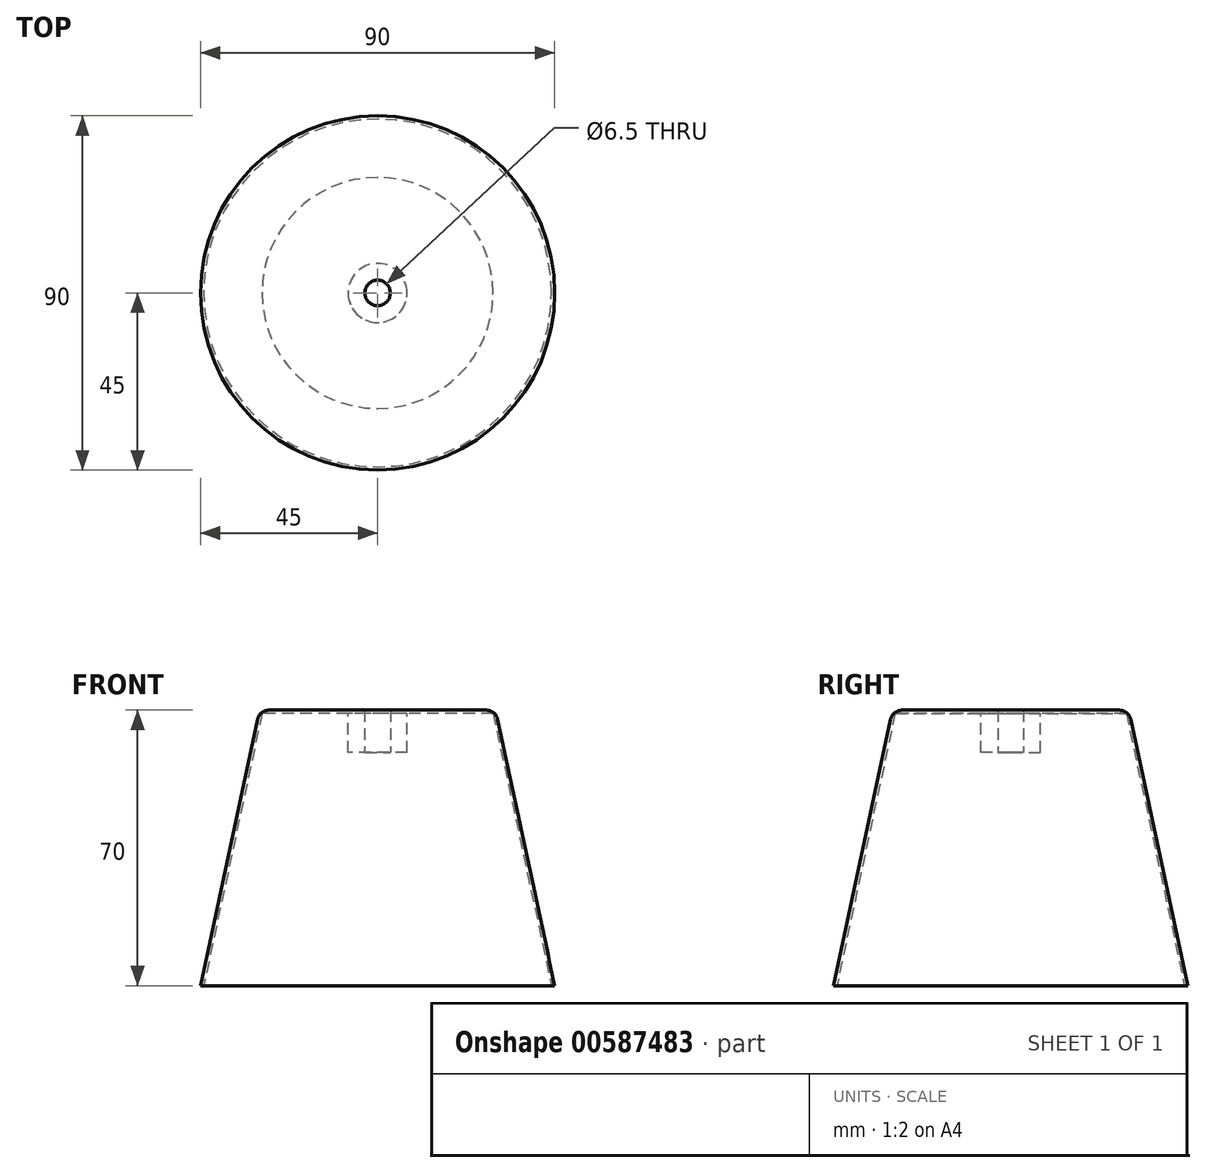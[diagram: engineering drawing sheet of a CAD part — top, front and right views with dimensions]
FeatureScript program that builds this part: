
annotation { "Feature Type Name" : "Feature", "Feature Type Description" : "" }
export const myFeature = defineFeature(function(context is Context, id is Id, definition is map)
    precondition{}
    {
        {
            var Q0;
            Q0=qCreatedBy(makeId("Top.planeOp"),FACE);
            cPlane(context, id + "F0", {"entities" : qUnion([Q0]), "cplaneType" : CPlaneType.OFFSET, "offset" : 70 * mm, "width" : 150 * mm, "height" : 150 * mm});
        }
        {
            var Q0;
            Q0=qCreatedBy(makeId("Top.planeOp"),FACE);
            var sketch = newSketch(context, id + "F1", { "sketchPlane" : qUnion([Q0])});
            skCircle(sketch, "E0", {"center": v(0, 0) * mm, "radius": 45 * mm});
            skSolve(sketch);
        }
        {
            var Q0;
            Q0=qCreatedBy(id+"F0.planeOp",FACE);
            var sketch = newSketch(context, id + "F2", { "sketchPlane" : qUnion([Q0])});
            skCircle(sketch, "E1", {"center": v(0, 0) * mm, "radius": 30 * mm});
            skSolve(sketch);
        }
        {
            var Q0;
            Q0=makeQuery(id+"F1.imprint","IMPRINT",FACE,{"disambiguationData":[TD([[makeQuery(id+"F1.imprint","IMPRINT",EDGE,{"derivedFrom":sQuery(id+"F1.wireOp",EDGE,"E0")}),1.0]])]});
            var Q1;
            Q1=makeQuery(id+"F2.imprint","IMPRINT",FACE,{"disambiguationData":[TD([[makeQuery(id+"F2.imprint","IMPRINT",EDGE,{"derivedFrom":sQuery(id+"F2.wireOp",EDGE,"E1")}),1.0]])]});
            var Q2;
            Q2=makeQuery(id+"F1.imprint","IMPRINT",FACE,{"disambiguationData":[TD([[makeQuery(id+"F1.imprint","IMPRINT",EDGE,{"derivedFrom":sQuery(id+"F1.wireOp",EDGE,"E0")}),1.0]])]});
            var Q3;
            Q3=makeQuery(id+"F2.imprint","IMPRINT",FACE,{"disambiguationData":[TD([[makeQuery(id+"F2.imprint","IMPRINT",EDGE,{"derivedFrom":sQuery(id+"F2.wireOp",EDGE,"E1")}),1.0]])]});
            loft(context, id + "F3", {"sheetProfilesArray" : [{ "sheetProfileEntities" : qUnion([Q0]) }, { "sheetProfileEntities" : qUnion([Q1]) }], "wireProfilesArray" : [{ "wireProfileEntities" : qUnion([Q2]) }, { "wireProfileEntities" : qUnion([Q3]) }]});
        }
        {
            var Q0;
            Q0=makeQuery(id+"F3.opLoft","CAP_FACE",FACE,{"disambiguationData":[OSD([makeQuery(id+"F1.imprint","IMPRINT",FACE,{"disambiguationData":[TD([[makeQuery(id+"F1.imprint","IMPRINT",EDGE,{"derivedFrom":sQuery(id+"F1.wireOp",EDGE,"E0")}),1.0]])]})])],"isStart":true});
            shell(context, id + "F4", {"entities" : qUnion([Q0]), "thickness" : .8 * mm});
        }
        {
            var Q0;
            Q0=makeQuery(id+"F4.opShell","OFFSET_FACE",FACE,{"disambiguationData":[OSD([makeQuery(id+"F2.imprint","IMPRINT",FACE,{"disambiguationData":[TD([[makeQuery(id+"F2.imprint","IMPRINT",EDGE,{"derivedFrom":sQuery(id+"F2.wireOp",EDGE,"E1")}),1.0]])]})])]});
            var sketch = newSketch(context, id + "F5", { "sketchPlane" : qUnion([Q0])});
            skCircle(sketch, "E2", {"center": v(0, 0) * mm, "radius": 7.5 * mm});
            skSolve(sketch);
        }
        {
            var Q0;
            Q0=makeQuery(id+"F5.imprint","IMPRINT",FACE,{"disambiguationData":[TD([[makeQuery(id+"F5.imprint","IMPRINT",EDGE,{"derivedFrom":sQuery(id+"F5.wireOp",EDGE,"E2")}),1.0]])]});
            extrude(context, id + "F6", {"entities" : qUnion([Q0]), "operationType" : NewBodyOperationType.ADD, "depth" : 10 * mm, "offsetDistance" : 25 * mm});
        }
        {
            var Q0;
            Q0=makeQuery(id+"F6.opExtrude","CAP_FACE",FACE,{"disambiguationData":[OSD([sQuery(id+"F5.wireOp",EDGE,"E2")])],"isStart":false});
            var sketch = newSketch(context, id + "F7", { "sketchPlane" : qUnion([Q0])});
            skCircle(sketch, "E3", {"center": v(0, 0) * mm, "radius": 3.25 * mm});
            skSolve(sketch);
        }
        {
            var Q0;
            Q0=makeQuery(id+"F7.imprint","IMPRINT",FACE,{"disambiguationData":[TD([[makeQuery(id+"F7.imprint","IMPRINT",EDGE,{"derivedFrom":sQuery(id+"F7.wireOp",EDGE,"E3")}),1.0]])]});
            extrude(context, id + "F8", {"entities" : qUnion([Q0]), "operationType" : NewBodyOperationType.REMOVE, "endBound" : BoundingType.THROUGH_ALL, "oppositeDirection" : true, "depth" : 25 * mm, "offsetDistance" : 25 * mm});
        }
        {
            var Q0;
            Q0=makeQuery(id+"F3.opLoft","MID_CAP_EDGE",EDGE,{"disambiguationData":[OSD([sQuery(id+"F1.wireOp",EDGE,"E0"),sQuery(id+"F2.wireOp",EDGE,"E1")])],"capPos":1.0});
            fillet(context, id + "F9", {"entities" : qUnion([Q0]), "radius" : 3 * mm, "tangentPropagation" : true, "allowEdgeOverflow" : false});
        }
    });
